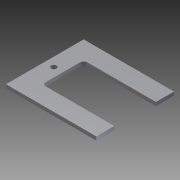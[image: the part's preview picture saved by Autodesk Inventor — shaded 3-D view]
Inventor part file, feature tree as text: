
AUTODESK INVENTOR PART (.ipt)
format: ipt  version: 2012 (Build 160160000, 160)  size: 83,968 bytes
history: native  units: mm
features: extrude x1, sketch x1
ambient origin geometry x8: Origin, YZ Plane, XZ Plane, XY Plane, X Axis, Y Axis, Z Axis, Center Point
bodies: Solid1 (feature_tree)
feature tree (2):
  extrude  "Extrusion1"  Depth=2.0mm TaperAngle=0.0deg
  sketch  "Sketch1"  dims[d0=40.0mm d1=23.0mm d2=2.0mm d3=10.0mm d4=50.0mm d5=43.0mm d6=3.0mm d7=5.0mm d8=21.5mm d9=2.0mm d10=0.0mm]
